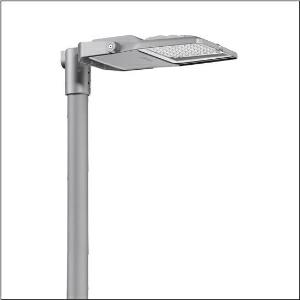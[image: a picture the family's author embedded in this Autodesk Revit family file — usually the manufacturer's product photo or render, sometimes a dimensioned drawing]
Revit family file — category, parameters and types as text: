
# Revit family: floodlight_fl_21_iq_mini___pl52_5xa7771c4d3a_e4a2
name_source: partatom
category: Lighting Fixtures
units: mm (PartAtom-declared; Revit-internal decimal feet)

## family parameters
Cut with Voids When Loaded = No
Host = Face
Light Source = No
Part Type = Normal
Room Calculation Point = No
Round Connector Dimension = Use Diameter
Shared = No

## types (1)
- --- (1 x LED, 12720 lm, 87.2 W, 4000K)
    Apparent Load = 87 VA
    CIE Flux Codes = 26 60 98 100 100
    Color Rendering = 70
    Color Temperature = 4000K
    Default Elevation = 1800 mm
    Description = Floodlight FL 21 iQ mini, floodlight, primary light control with lens, of PMMA, primary optical cover: protective disc, of toughened safety glass, transparent, light distribution: PL52, light emission: direct distribution, installation type: surface-mounted, LED, High Power LED, rated luminous flux: 12.720lm, luminous efficacy: 146lm/W, light colour: 740, colour temperature: 4000K, control: Auto-Match, Temp-Guard, Lumen-Switch, Night-Set, Smart-Wire, Light-Fading, Desk-Remote (wireless, voltage-free reading and setting of iQ features in the workshop via application-optimized NFC function/RFID function), optimised constant luminous flux control (CLO 2.0), with terminal, 6-pole, mains connection: 220..240V, AC, 50/60Hz, start of lifetime: 87W, end of service life: 92W, reduction: 40W, luminaire housing, of diecast aluminium, powder-coated, Siteco® metallic grey (DB 702S), corrosivity category C5 mid according to DIN EN ISO 12944, sealing non-destructively replaceable, please order mast flange separately, mast bracket, of steel, galvanised, powder-coated, Siteco® metallic grey (DB 702S), protection rating (complete): IP66, insulation class (complete): insulation class II (safety insulation), certification: CE, ENEC, VDE, protection symbol: D, impact resistance: IK08, permissible operating ambient temperature: -40..+40°C, permissible operating ambient temperature for outdoor applications: -40..+50°C, standard: DIN EN 12944, LABS conformity tested according to VDMA 24364:2018-05, packaging unit: 1 piece

Light Distribution: PL52
    Height = 70 mm
    Lamp = 1 x LED
    Lamp Light Flux = 12720 lm
    Lamp Power = 87.2 W
    Lamp count = 1
    Length = 485 mm
    Luminous efficacy = 146 lm/W
    Manufacturer = Siteco
    ModVariant = No
    Model = 5XA7771C4D3A
    Number of Poles = 1
    OnlyDefault = Yes
    Power Factor = 1
    Product Name = Floodlight FL 21 iQ mini | PL52
    Product group = floodlight | pylon annexe
    ProductGroupID = 6200
    Protection Class = Protection class II
    Protection Degree = IP 66
    RLX_Detail_Level = 1
    RLX_Emergency_Light_Flux = 0 lm
    RLX_Emergency_Type = 0
    RLX_Emergency_Type_DB = No
    RlxData = <blob elided: 101421 chars, md5=5dd286cc>
    Socket = socket
    Standby Power = 0 W
    System Light Flux = 12720 lm
    System Power = 87 W
    Type Comments = factory setting: luminous flux: 100 % | dim-lin: 254 | 456 mA
    Type Image = l_1007125.jpg
    URL = http://relux.com
    VarID = @adj_114599
    Voltage = 0 V
    Weight = 0.00 kg
    Width = 337 mm

## geometry (parser evidence)
native form markers: Blend x4, Sweep x14
no freeform markers — native parametric forms only
